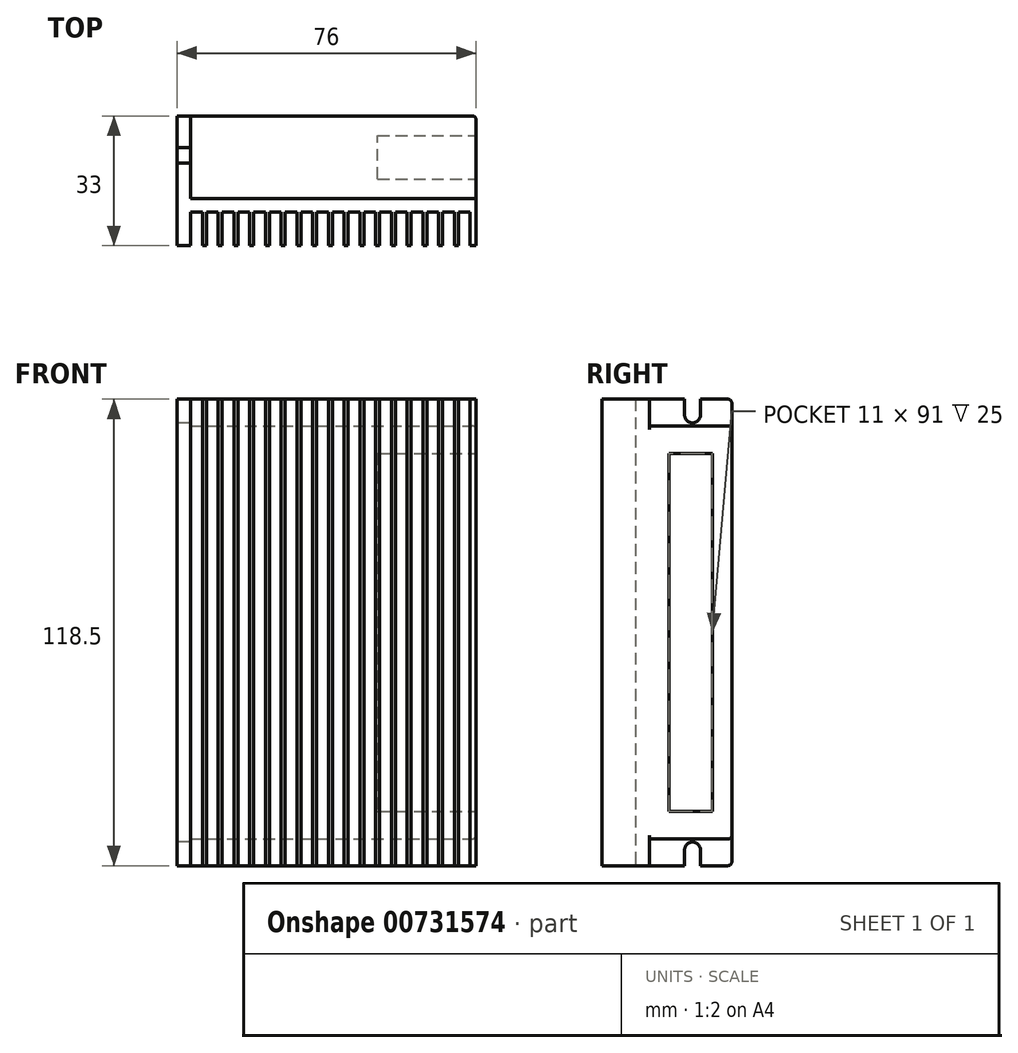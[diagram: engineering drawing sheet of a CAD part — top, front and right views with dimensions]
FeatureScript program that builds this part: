
annotation { "Feature Type Name" : "Feature", "Feature Type Description" : "" }
export const myFeature = defineFeature(function(context is Context, id is Id, definition is map)
    precondition{}
    {
        {
            var Q0;
            Q0=qCreatedBy(makeId("Front.planeOp"),FACE);
            var sketch = newSketch(context, id + "F0", { "sketchPlane" : qUnion([Q0])});
            skLineSegment(sketch, "E0.bottom", {"start": v(-38, 59.25) * mm, "end": v(38, 59.25) * mm});
            skLineSegment(sketch, "E0.top", {"start": v(-38, -59.25) * mm, "end": v(38, -59.25) * mm});
            skLineSegment(sketch, "E0.left", {"start": v(-38, 59.25) * mm, "end": v(-38, -59.25) * mm});
            skLineSegment(sketch, "E0.right", {"start": v(38, 59.25) * mm, "end": v(38, -59.25) * mm});
            skLineSegment(sketch, "E1", {"start": v(-38, 0) * mm, "end": v(38, 0) * mm, "construction": true});
            skLineSegment(sketch, "E2", {"start": v(0, 59.25) * mm, "end": v(0, -59.25) * mm, "construction": true});
            skSolve(sketch);
        }
        {
            var Q0;
            Q0=qCreatedBy(makeId("Top.planeOp"),FACE);
            var sketch = newSketch(context, id + "F1", { "sketchPlane" : qUnion([Q0])});
            skLineSegment(sketch, "E3.bottom", {"start": v(-38, 16.5) * mm, "end": v(38, 16.5) * mm});
            skLineSegment(sketch, "E3.top", {"start": v(-38, -16.5) * mm, "end": v(-34.5, -16.5) * mm});
            skLineSegment(sketch, "E3.left", {"start": v(-38, 16.5) * mm, "end": v(-38, -16.5) * mm});
            skLineSegment(sketch, "E3.right", {"start": v(38, 16.5) * mm, "end": v(38, -16.5) * mm});
            skLineSegment(sketch, "E4", {"start": v(-34.5, 16.5) * mm, "end": v(-34.5, -4.5) * mm});
            skLineSegment(sketch, "E5", {"start": v(-34.5, -4.5) * mm, "end": v(38, -4.5) * mm});
            skLineSegment(sketch, "E6", {"start": v(-34.5, -16.5) * mm, "end": v(-34.5, -8) * mm});
            skLineSegment(sketch, "E7", {"start": v(-34.5, -4.5) * mm, "end": v(-34.5, -8) * mm, "construction": true});
            skLineSegment(sketch, "E8", {"start": v(-34.5, -8) * mm, "end": v(-31.5, -8) * mm});
            skLineSegment(sketch, "E9", {"start": v(-31.5, -8) * mm, "end": v(-31.5, -16.5) * mm});
            skLineSegment(sketch, "E10", {"start": v(-31.5, -16.5) * mm, "end": v(-30.5, -16.5) * mm});
            skLineSegment(sketch, "E11", {"start": v(-30.5, -16.5) * mm, "end": v(-30.5, -8) * mm});
            skLineSegment(sketch, "E12.1.0.0", {"start": v(-30.5, -8) * mm, "end": v(-27.5, -8) * mm});
            skLineSegment(sketch, "E12.1.0.1", {"start": v(-27.5, -8) * mm, "end": v(-27.5, -16.5) * mm});
            skLineSegment(sketch, "E12.1.0.2", {"start": v(-26.5, -16.5) * mm, "end": v(-26.5, -8) * mm});
            skLineSegment(sketch, "E12.1.0.3", {"start": v(-27.5, -16.5) * mm, "end": v(-26.5, -16.5) * mm});
            skLineSegment(sketch, "E12.2.0.0", {"start": v(-26.5, -8) * mm, "end": v(-23.5, -8) * mm});
            skLineSegment(sketch, "E12.2.0.1", {"start": v(-23.5, -8) * mm, "end": v(-23.5, -16.5) * mm});
            skLineSegment(sketch, "E12.2.0.2", {"start": v(-22.5, -16.5) * mm, "end": v(-22.5, -8) * mm});
            skLineSegment(sketch, "E12.2.0.3", {"start": v(-23.5, -16.5) * mm, "end": v(-22.5, -16.5) * mm});
            skLineSegment(sketch, "E12.3.0.0", {"start": v(-22.5, -8) * mm, "end": v(-19.5, -8) * mm});
            skLineSegment(sketch, "E12.3.0.1", {"start": v(-19.5, -8) * mm, "end": v(-19.5, -16.5) * mm});
            skLineSegment(sketch, "E12.3.0.2", {"start": v(-18.5, -16.5) * mm, "end": v(-18.5, -8) * mm});
            skLineSegment(sketch, "E12.3.0.3", {"start": v(-19.5, -16.5) * mm, "end": v(-18.5, -16.5) * mm});
            skLineSegment(sketch, "E12.4.0.0", {"start": v(-18.5, -8) * mm, "end": v(-15.5, -8) * mm});
            skLineSegment(sketch, "E12.4.0.1", {"start": v(-15.5, -8) * mm, "end": v(-15.5, -16.5) * mm});
            skLineSegment(sketch, "E12.4.0.2", {"start": v(-14.5, -16.5) * mm, "end": v(-14.5, -8) * mm});
            skLineSegment(sketch, "E12.4.0.3", {"start": v(-15.5, -16.5) * mm, "end": v(-14.5, -16.5) * mm});
            skLineSegment(sketch, "E12.5.0.0", {"start": v(-14.5, -8) * mm, "end": v(-11.5, -8) * mm});
            skLineSegment(sketch, "E12.5.0.1", {"start": v(-11.5, -8) * mm, "end": v(-11.5, -16.5) * mm});
            skLineSegment(sketch, "E12.5.0.2", {"start": v(-10.5, -16.5) * mm, "end": v(-10.5, -8) * mm});
            skLineSegment(sketch, "E12.5.0.3", {"start": v(-11.5, -16.5) * mm, "end": v(-10.5, -16.5) * mm});
            skLineSegment(sketch, "E12.6.0.0", {"start": v(-10.5, -8) * mm, "end": v(-7.5, -8) * mm});
            skLineSegment(sketch, "E12.6.0.1", {"start": v(-7.5, -8) * mm, "end": v(-7.5, -16.5) * mm});
            skLineSegment(sketch, "E12.6.0.2", {"start": v(-6.5, -16.5) * mm, "end": v(-6.5, -8) * mm});
            skLineSegment(sketch, "E12.6.0.3", {"start": v(-7.5, -16.5) * mm, "end": v(-6.5, -16.5) * mm});
            skLineSegment(sketch, "E12.7.0.0", {"start": v(-6.5, -8) * mm, "end": v(-3.5, -8) * mm});
            skLineSegment(sketch, "E12.7.0.1", {"start": v(-3.5, -8) * mm, "end": v(-3.5, -16.5) * mm});
            skLineSegment(sketch, "E12.7.0.2", {"start": v(-2.5, -16.5) * mm, "end": v(-2.5, -8) * mm});
            skLineSegment(sketch, "E12.7.0.3", {"start": v(-3.5, -16.5) * mm, "end": v(-2.5, -16.5) * mm});
            skLineSegment(sketch, "E12.8.0.0", {"start": v(-2.5, -8) * mm, "end": v(0.5, -8) * mm});
            skLineSegment(sketch, "E12.8.0.1", {"start": v(0.5, -8) * mm, "end": v(0.5, -16.5) * mm});
            skLineSegment(sketch, "E12.8.0.2", {"start": v(1.5, -16.5) * mm, "end": v(1.5, -8) * mm});
            skLineSegment(sketch, "E12.8.0.3", {"start": v(0.5, -16.5) * mm, "end": v(1.5, -16.5) * mm});
            skLineSegment(sketch, "E12.9.0.0", {"start": v(1.5, -8) * mm, "end": v(4.5, -8) * mm});
            skLineSegment(sketch, "E12.9.0.1", {"start": v(4.5, -8) * mm, "end": v(4.5, -16.5) * mm});
            skLineSegment(sketch, "E12.9.0.2", {"start": v(5.5, -16.5) * mm, "end": v(5.5, -8) * mm});
            skLineSegment(sketch, "E12.9.0.3", {"start": v(4.5, -16.5) * mm, "end": v(5.5, -16.5) * mm});
            skLineSegment(sketch, "E12.10.0.0", {"start": v(5.5, -8) * mm, "end": v(8.5, -8) * mm});
            skLineSegment(sketch, "E12.10.0.1", {"start": v(8.5, -8) * mm, "end": v(8.5, -16.5) * mm});
            skLineSegment(sketch, "E12.10.0.2", {"start": v(9.5, -16.5) * mm, "end": v(9.5, -8) * mm});
            skLineSegment(sketch, "E12.10.0.3", {"start": v(8.5, -16.5) * mm, "end": v(9.5, -16.5) * mm});
            skLineSegment(sketch, "E12.11.0.0", {"start": v(9.5, -8) * mm, "end": v(12.5, -8) * mm});
            skLineSegment(sketch, "E12.11.0.1", {"start": v(12.5, -8) * mm, "end": v(12.5, -16.5) * mm});
            skLineSegment(sketch, "E12.11.0.2", {"start": v(13.5, -16.5) * mm, "end": v(13.5, -8) * mm});
            skLineSegment(sketch, "E12.11.0.3", {"start": v(12.5, -16.5) * mm, "end": v(13.5, -16.5) * mm});
            skLineSegment(sketch, "E12.12.0.0", {"start": v(13.5, -8) * mm, "end": v(16.5, -8) * mm});
            skLineSegment(sketch, "E12.12.0.1", {"start": v(16.5, -8) * mm, "end": v(16.5, -16.5) * mm});
            skLineSegment(sketch, "E12.12.0.2", {"start": v(17.5, -16.5) * mm, "end": v(17.5, -8) * mm});
            skLineSegment(sketch, "E12.12.0.3", {"start": v(16.5, -16.5) * mm, "end": v(17.5, -16.5) * mm});
            skLineSegment(sketch, "E12.13.0.0", {"start": v(17.5, -8) * mm, "end": v(20.5, -8) * mm});
            skLineSegment(sketch, "E12.13.0.1", {"start": v(20.5, -8) * mm, "end": v(20.5, -16.5) * mm});
            skLineSegment(sketch, "E12.13.0.2", {"start": v(21.5, -16.5) * mm, "end": v(21.5, -8) * mm});
            skLineSegment(sketch, "E12.13.0.3", {"start": v(20.5, -16.5) * mm, "end": v(21.5, -16.5) * mm});
            skLineSegment(sketch, "E12.14.0.0", {"start": v(21.5, -8) * mm, "end": v(24.5, -8) * mm});
            skLineSegment(sketch, "E12.14.0.1", {"start": v(24.5, -8) * mm, "end": v(24.5, -16.5) * mm});
            skLineSegment(sketch, "E12.14.0.2", {"start": v(25.5, -16.5) * mm, "end": v(25.5, -8) * mm});
            skLineSegment(sketch, "E12.14.0.3", {"start": v(24.5, -16.5) * mm, "end": v(25.5, -16.5) * mm});
            skLineSegment(sketch, "E12.15.0.0", {"start": v(25.5, -8) * mm, "end": v(28.5, -8) * mm});
            skLineSegment(sketch, "E12.15.0.1", {"start": v(28.5, -8) * mm, "end": v(28.5, -16.5) * mm});
            skLineSegment(sketch, "E12.15.0.2", {"start": v(29.5, -16.5) * mm, "end": v(29.5, -8) * mm});
            skLineSegment(sketch, "E12.15.0.3", {"start": v(28.5, -16.5) * mm, "end": v(29.5, -16.5) * mm});
            skLineSegment(sketch, "E12.16.0.0", {"start": v(29.5, -8) * mm, "end": v(32.5, -8) * mm});
            skLineSegment(sketch, "E12.16.0.1", {"start": v(32.5, -8) * mm, "end": v(32.5, -16.5) * mm});
            skLineSegment(sketch, "E12.16.0.2", {"start": v(33.5, -16.5) * mm, "end": v(33.5, -8) * mm});
            skLineSegment(sketch, "E12.16.0.3", {"start": v(32.5, -16.5) * mm, "end": v(33.5, -16.5) * mm});
            skLineSegment(sketch, "E12.17.0.0", {"start": v(33.5, -8) * mm, "end": v(36.5, -8) * mm});
            skLineSegment(sketch, "E12.17.0.1", {"start": v(36.5, -8) * mm, "end": v(36.5, -16.5) * mm});
            skLineSegment(sketch, "E12.direction1", {"start": v(-34.5, -8) * mm, "end": v(-30.5, -8) * mm, "construction": true});
            skLineSegment(sketch, "E13", {"start": v(36.5, -16.5) * mm, "end": v(38, -16.5) * mm});
            skSolve(sketch);
        }
        {
            var Q0;
            Q0=makeQuery(id+"F1.imprint","IMPRINT",FACE,{"disambiguationData":[TD([[makeQuery(id+"F1.imprint","IMPRINT",EDGE,{"derivedFrom":sQuery(id+"F1.wireOp",EDGE,"E3.top")}),1.0]])]});
            extrude(context, id + "F2", {"entities" : qUnion([Q0]), "depth" : 118.5 * mm, "offsetDistance" : 25 * mm, "symmetric" : true});
        }
        {
            var Q0;
            {var subQ3=sQuery(id+"F1.wireOp",EDGE,"E4");Q0=makeQuery(id+"F1.imprint","IMPRINT",FACE,{"disambiguationData":[TD([[makeQuery(id+"F1.imprint","IMPRINT",EDGE,{"derivedFrom":subQ3}),1.0]])]});}
            extrude(context, id + "F3", {"entities" : qUnion([Q0]), "operationType" : NewBodyOperationType.ADD, "depth" : 105 * mm, "offsetDistance" : 25 * mm, "symmetric" : true});
        }
        {
            var Q0;
            Q0=makeQuery(id+"F2.opExtrude","SWEPT_FACE",FACE,{"disambiguationData":[OSD([sQuery(id+"F1.wireOp",EDGE,"E3.left")])]});
            var sketch = newSketch(context, id + "F4", { "sketchPlane" : qUnion([Q0])});
            skLineSegment(sketch, "E14.bottom", {"start": v(-8.5, 59.25) * mm, "end": v(-4.5, 59.25) * mm});
            skLineSegment(sketch, "E14.left", {"start": v(-8.5, 59.25) * mm, "end": v(-8.5, 55.25) * mm});
            skLineSegment(sketch, "E14.right", {"start": v(-4.5, 59.25) * mm, "end": v(-4.5, 55.25) * mm});
            skArc(sketch, "E15", {"start": v(-8.5, 55.25) * mm, "mid": v(-6.5, 53.25) * mm, "end": v(-4.5, 55.25) * mm});
            skLineSegment(sketch, "E16", {"start": v(-6.5, 59.25) * mm, "end": v(-6.5, 55.25) * mm, "construction": true});
            skLineSegment(sketch, "E17", {"start": v(-16.5, 0) * mm, "end": v(16.5, 0) * mm, "construction": true});
            skLineSegment(sketch, "E18.MirrorCS", {"start": v(-8.5, -59.25) * mm, "end": v(-4.5, -59.25) * mm});
            skLineSegment(sketch, "E19.MirrorCS", {"start": v(-4.5, -59.25) * mm, "end": v(-4.5, -55.25) * mm});
            skArc(sketch, "E20.MirrorCS", {"start": v(-8.5, -55.25) * mm, "mid": v(-6.5, -53.25) * mm, "end": v(-4.5, -55.25) * mm});
            skLineSegment(sketch, "E21.MirrorCS", {"start": v(-8.5, -59.25) * mm, "end": v(-8.5, -55.25) * mm});
            skLineSegment(sketch, "E22.MirrorCS", {"start": v(-6.5, -59.25) * mm, "end": v(-6.5, -55.25) * mm, "construction": true});
            skSolve(sketch);
        }
        {
            var Q0;
            Q0 = qSketchRegion(id + "F4", true);
            var Q1;
            {var subQ0=sQuery(id+"F1.wireOp",EDGE,"E5");var subQ1=sQuery(id+"F1.wireOp",EDGE,"E3.bottom");var subQ2=sQuery(id+"F1.wireOp",EDGE,"E4");var subQ3=sQuery(id+"F1.wireOp",EDGE,"E3.right");Q1=makeQuery(id+"F3.boolean.opBoolean","SPLIT",FACE,{"disambiguationData":[TD([makeQuery(id+"F3.opExtrude","CAP_FACE",FACE,{"disambiguationData":[OSD([subQ1,subQ3,subQ2,subQ0])],"isStart":true})])],"derivedFrom":makeQuery(id+"F2.opExtrude","SWEPT_FACE",FACE,{"disambiguationData":[OSD([subQ2])]})});}
            extrude(context, id + "F5", {"entities" : qUnion([Q0]), "operationType" : NewBodyOperationType.REMOVE, "endBound" : BoundingType.UP_TO_SURFACE, "oppositeDirection" : true, "depth" : 25 * mm, "endBoundEntityFace" : qUnion([Q1]), "offsetDistance" : 25 * mm});
        }
        {
            var Q0;
            {var subQ0=sQuery(id+"F1.wireOp",EDGE,"E3.right");Q0=makeQuery(id+"F3.boolean.opBoolean","MERGE",FACE,{"derivedFrom":[makeQuery(id+"F2.opExtrude","SWEPT_FACE",FACE,{"disambiguationData":[OSD([subQ0])]}),makeQuery(id+"F3.opExtrude","SWEPT_FACE",FACE,{"disambiguationData":[OSD([subQ0])]})]});}
            var sketch = newSketch(context, id + "F6", { "sketchPlane" : qUnion([Q0])});
            skLineSegment(sketch, "E23.bottom", {"start": v(0.5, 45.5) * mm, "end": v(11.5, 45.5) * mm});
            skLineSegment(sketch, "E23.top", {"start": v(0.5, -45.5) * mm, "end": v(11.5, -45.5) * mm});
            skLineSegment(sketch, "E23.left", {"start": v(0.5, 45.5) * mm, "end": v(0.5, -45.5) * mm});
            skLineSegment(sketch, "E23.right", {"start": v(11.5, 45.5) * mm, "end": v(11.5, -45.5) * mm});
            skSolve(sketch);
        }
        {
            var Q0;
            Q0 = qSketchRegion(id + "F6", true);
            extrude(context, id + "F7", {"entities" : qUnion([Q0]), "operationType" : NewBodyOperationType.REMOVE, "oppositeDirection" : true, "depth" : 25 * mm, "offsetDistance" : 25 * mm});
        }
        {
            var Q0;
            Q0=makeQuery(id+"F3.opExtrude","CAP_EDGE",EDGE,{"disambiguationData":[OSD([sQuery(id+"F1.wireOp",EDGE,"E3.right")])],"isStart":false});
            var Q1;
            Q1=makeQuery(id+"F3.opExtrude","CAP_EDGE",EDGE,{"disambiguationData":[OSD([sQuery(id+"F1.wireOp",EDGE,"E3.bottom")])],"isStart":false});
            var Q2;
            Q2=makeQuery(id+"F3.opExtrude","SWEPT_EDGE",EDGE,{"disambiguationData":[OSD([sQuery(id+"F1.wireOp",EDGE,"E3.bottom"),sQuery(id+"F1.wireOp",EDGE,"E3.right")])]});
            var Q3;
            Q3=makeQuery(id+"F2.opExtrude","CAP_EDGE",EDGE,{"disambiguationData":[OSD([sQuery(id+"F1.wireOp",EDGE,"E3.bottom")])],"isStart":false});
            var Q4;
            Q4=makeQuery(id+"F3.opExtrude","CAP_EDGE",EDGE,{"disambiguationData":[OSD([sQuery(id+"F1.wireOp",EDGE,"E3.bottom")])],"isStart":true});
            var Q5;
            Q5=makeQuery(id+"F3.opExtrude","CAP_EDGE",EDGE,{"disambiguationData":[OSD([sQuery(id+"F1.wireOp",EDGE,"E3.right")])],"isStart":true});
            var Q6;
            Q6=makeQuery(id+"F2.opExtrude","CAP_EDGE",EDGE,{"disambiguationData":[OSD([sQuery(id+"F1.wireOp",EDGE,"E3.bottom")])],"isStart":true});
            fillet(context, id + "F8", {"entities" : qUnion([Q0, Q1, Q2, Q3, Q4, Q5, Q6]), "radius" : 1 * mm, "tangentPropagation" : true, "allowEdgeOverflow" : false});
        }
    });
